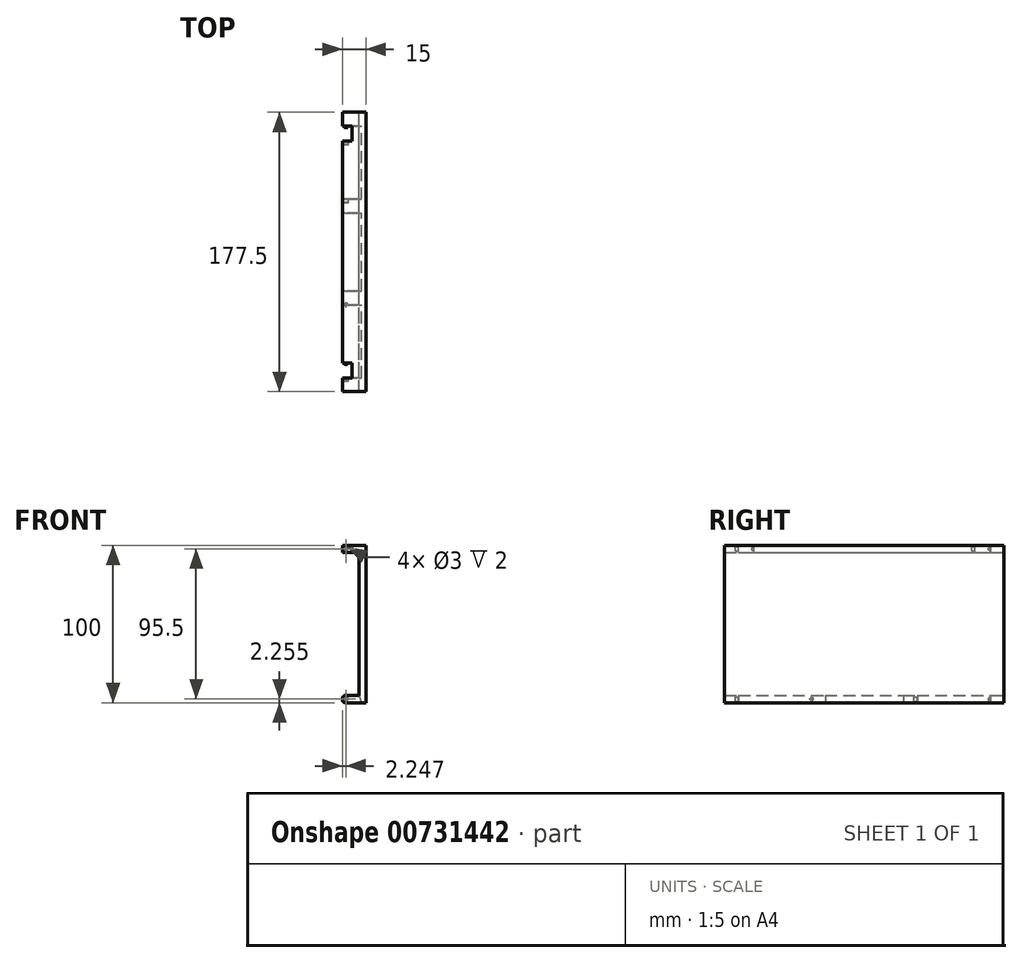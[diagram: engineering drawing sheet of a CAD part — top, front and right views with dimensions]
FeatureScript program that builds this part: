
annotation { "Feature Type Name" : "Feature", "Feature Type Description" : "" }
export const myFeature = defineFeature(function(context is Context, id is Id, definition is map)
    precondition{}
    {
        {
            var Q0;
            Q0=qCreatedBy(makeId("Front.planeOp"),FACE);
            var sketch = newSketch(context, id + "F0", { "sketchPlane" : qUnion([Q0])});
            skLineSegment(sketch, "E0", {"start": v(5.92, -29.22) * mm, "end": v(5.92, 61.78) * mm});
            skLineSegment(sketch, "E1", {"start": v(5.92, 61.78) * mm, "end": v(-4.58, 61.78) * mm});
            skLineSegment(sketch, "E2", {"start": v(-4.58, 61.78) * mm, "end": v(-4.58, 66.28) * mm});
            skLineSegment(sketch, "E3", {"start": v(-4.58, 66.28) * mm, "end": v(10.42, 66.28) * mm});
            skLineSegment(sketch, "E4", {"start": v(10.42, 66.28) * mm, "end": v(10.42, -33.72) * mm});
            skLineSegment(sketch, "E5", {"start": v(-4.58, 66.28) * mm, "end": v(-0.08, 66.28) * mm});
            skPoint(sketch, "E6.visualSharp", {"position": v(-0.08, -33.72) * mm});
            skPoint(sketch, "E7.visualSharp", {"position": v(-4.58, -29.22) * mm});
            skLineSegment(sketch, "E8", {"start": v(5.92, -29.22) * mm, "end": v(-2.88, -29.22) * mm});
            skLineSegment(sketch, "E9", {"start": v(0.67, -29.22) * mm, "end": v(0.67, -33.72) * mm});
            skCircle(sketch, "E10", {"center": v(-2.33, -31.47) * mm, "radius": 1.5 * mm});
            skCircle(sketch, "E11", {"center": v(-2.33, -31.47) * mm, "radius": 1.3 * mm});
            skCircle(sketch, "E12", {"center": v(-2.33, 64.03) * mm, "radius": 1.3 * mm});
            skCircle(sketch, "E13", {"center": v(-2.33, 64.03) * mm, "radius": 1.5 * mm});
            skLineSegment(sketch, "E14", {"start": v(-4.58, -31.47) * mm, "end": v(-4.58, -31.47) * mm});
            skPoint(sketch, "E15.visualSharp", {"position": v(-4.58, -33.72) * mm});
            skLineSegment(sketch, "E16", {"start": v(0.67, -33.72) * mm, "end": v(10.42, -33.72) * mm});
            skLineSegment(sketch, "E17", {"start": v(-4.58, -30.92) * mm, "end": v(-4.58, -32.02) * mm});
            skLineSegment(sketch, "E18", {"start": v(0.67, -33.72) * mm, "end": v(-2.88, -33.72) * mm});
            skArc(sketch, "E19.filletArc", {"start": v(-2.88, -29.22) * mm, "mid": v(-4.09, -29.71) * mm, "end": v(-4.58, -30.92) * mm});
            skArc(sketch, "E20.filletArc", {"start": v(-4.58, -32.02) * mm, "mid": v(-4.09, -33.22) * mm, "end": v(-2.88, -33.72) * mm});
            skLineSegment(sketch, "E21", {"start": v(5.92, -29.22) * mm, "end": v(5.92, -33.72) * mm});
            skLineSegment(sketch, "E22", {"start": v(5.92, -29.22) * mm, "end": v(7.53, -33.72) * mm});
            skLineSegment(sketch, "E23", {"start": v(7.53, -33.72) * mm, "end": v(10.42, -33.72) * mm});
            skLineSegment(sketch, "E24", {"start": v(1.42, 66.28) * mm, "end": v(1.42, 61.78) * mm});
            skSolve(sketch);
        }
        {
            var Q0;
            {var subQ0=sQuery(id+"F0.wireOp",EDGE,"E0");Q0=makeQuery(id+"F0.imprint","IMPRINT",FACE,{"disambiguationData":[TD([[makeQuery(id+"F0.imprint","IMPRINT",EDGE,{"derivedFrom":subQ0}),-1.0]])]});}
            var Q1;
            {var subQ0=sQuery(id+"F0.wireOp",EDGE,"E9");Q1=makeQuery(id+"F0.imprint","IMPRINT",FACE,{"disambiguationData":[TD([[makeQuery(id+"F0.imprint","IMPRINT",EDGE,{"derivedFrom":subQ0}),-1.0]])]});}
            var Q2;
            {var subQ2=sQuery(id+"F0.wireOp",EDGE,"E9");Q2=makeQuery(id+"F0.imprint","IMPRINT",FACE,{"disambiguationData":[TD([[makeQuery(id+"F0.imprint","IMPRINT",EDGE,{"derivedFrom":subQ2}),1.0]])]});}
            var Q3;
            {var subQ4=sQuery(id+"F0.wireOp",EDGE,"E21");Q3=makeQuery(id+"F0.imprint","IMPRINT",FACE,{"disambiguationData":[TD([[makeQuery(id+"F0.imprint","IMPRINT",EDGE,{"derivedFrom":subQ4}),1.0]])]});}
            var Q4;
            {var subQ3=sQuery(id+"F0.wireOp",EDGE,"E2");Q4=makeQuery(id+"F0.imprint","IMPRINT",FACE,{"disambiguationData":[TD([[makeQuery(id+"F0.imprint","IMPRINT",EDGE,{"derivedFrom":subQ3}),-1.0]])]});}
            extrude(context, id + "F1", {"entities" : qUnion([Q0, Q1, Q2, Q3, Q4]), "depth" : 177.5 * mm, "offsetDistance" : 25 * mm});
        }
        {
            var Q0;
            {var subQ2=sQuery(id+"F0.wireOp",EDGE,"E9");Q0=makeQuery(id+"F0.imprint","IMPRINT",FACE,{"disambiguationData":[TD([[makeQuery(id+"F0.imprint","IMPRINT",EDGE,{"derivedFrom":subQ2}),1.0]])]});}
            var Q1;
            {var subQ0=sQuery(id+"F0.wireOp",EDGE,"E9");Q1=makeQuery(id+"F0.imprint","IMPRINT",FACE,{"disambiguationData":[TD([[makeQuery(id+"F0.imprint","IMPRINT",EDGE,{"derivedFrom":subQ0}),-1.0]])]});}
            var Q2;
            {var subQ4=sQuery(id+"F0.wireOp",EDGE,"E21");Q2=makeQuery(id+"F0.imprint","IMPRINT",FACE,{"disambiguationData":[TD([[makeQuery(id+"F0.imprint","IMPRINT",EDGE,{"derivedFrom":subQ4}),1.0]])]});}
            extrude(context, id + "F2", {"entities" : qUnion([Q0, Q1, Q2]), "operationType" : NewBodyOperationType.REMOVE, "depth" : 168.7 * mm, "offsetDistance" : 25 * mm});
        }
        {
            var Q0;
            {var subQ2=sQuery(id+"F0.wireOp",EDGE,"E9");Q0=makeQuery(id+"F0.imprint","IMPRINT",FACE,{"disambiguationData":[TD([[makeQuery(id+"F0.imprint","IMPRINT",EDGE,{"derivedFrom":subQ2}),1.0]])]});}
            var Q1;
            {var subQ0=sQuery(id+"F0.wireOp",EDGE,"E9");Q1=makeQuery(id+"F0.imprint","IMPRINT",FACE,{"disambiguationData":[TD([[makeQuery(id+"F0.imprint","IMPRINT",EDGE,{"derivedFrom":subQ0}),-1.0]])]});}
            var Q2;
            {var subQ4=sQuery(id+"F0.wireOp",EDGE,"E21");Q2=makeQuery(id+"F0.imprint","IMPRINT",FACE,{"disambiguationData":[TD([[makeQuery(id+"F0.imprint","IMPRINT",EDGE,{"derivedFrom":subQ4}),1.0]])]});}
            extrude(context, id + "F3", {"entities" : qUnion([Q0, Q1, Q2]), "operationType" : NewBodyOperationType.ADD, "depth" : 122.3 * mm, "offsetDistance" : 25 * mm});
        }
        {
            var Q0;
            {var subQ2=sQuery(id+"F0.wireOp",EDGE,"E9");Q0=makeQuery(id+"F0.imprint","IMPRINT",FACE,{"disambiguationData":[TD([[makeQuery(id+"F0.imprint","IMPRINT",EDGE,{"derivedFrom":subQ2}),1.0]])]});}
            var Q1;
            {var subQ0=sQuery(id+"F0.wireOp",EDGE,"E9");Q1=makeQuery(id+"F0.imprint","IMPRINT",FACE,{"disambiguationData":[TD([[makeQuery(id+"F0.imprint","IMPRINT",EDGE,{"derivedFrom":subQ0}),-1.0]])]});}
            var Q2;
            {var subQ4=sQuery(id+"F0.wireOp",EDGE,"E21");Q2=makeQuery(id+"F0.imprint","IMPRINT",FACE,{"disambiguationData":[TD([[makeQuery(id+"F0.imprint","IMPRINT",EDGE,{"derivedFrom":subQ4}),1.0]])]});}
            extrude(context, id + "F4", {"entities" : qUnion([Q0, Q1, Q2]), "operationType" : NewBodyOperationType.REMOVE, "depth" : 113.5 * mm, "offsetDistance" : 25 * mm});
        }
        {
            var Q0;
            {var subQ2=sQuery(id+"F0.wireOp",EDGE,"E9");Q0=makeQuery(id+"F0.imprint","IMPRINT",FACE,{"disambiguationData":[TD([[makeQuery(id+"F0.imprint","IMPRINT",EDGE,{"derivedFrom":subQ2}),1.0]])]});}
            var Q1;
            {var subQ0=sQuery(id+"F0.wireOp",EDGE,"E9");Q1=makeQuery(id+"F0.imprint","IMPRINT",FACE,{"disambiguationData":[TD([[makeQuery(id+"F0.imprint","IMPRINT",EDGE,{"derivedFrom":subQ0}),-1.0]])]});}
            var Q2;
            {var subQ4=sQuery(id+"F0.wireOp",EDGE,"E21");Q2=makeQuery(id+"F0.imprint","IMPRINT",FACE,{"disambiguationData":[TD([[makeQuery(id+"F0.imprint","IMPRINT",EDGE,{"derivedFrom":subQ4}),1.0]])]});}
            extrude(context, id + "F5", {"entities" : qUnion([Q0, Q1, Q2]), "operationType" : NewBodyOperationType.ADD, "depth" : 64 * mm, "offsetDistance" : 25 * mm});
        }
        {
            var Q0;
            {var subQ2=sQuery(id+"F0.wireOp",EDGE,"E9");Q0=makeQuery(id+"F0.imprint","IMPRINT",FACE,{"disambiguationData":[TD([[makeQuery(id+"F0.imprint","IMPRINT",EDGE,{"derivedFrom":subQ2}),1.0]])]});}
            var Q1;
            {var subQ0=sQuery(id+"F0.wireOp",EDGE,"E9");Q1=makeQuery(id+"F0.imprint","IMPRINT",FACE,{"disambiguationData":[TD([[makeQuery(id+"F0.imprint","IMPRINT",EDGE,{"derivedFrom":subQ0}),-1.0]])]});}
            var Q2;
            {var subQ4=sQuery(id+"F0.wireOp",EDGE,"E21");Q2=makeQuery(id+"F0.imprint","IMPRINT",FACE,{"disambiguationData":[TD([[makeQuery(id+"F0.imprint","IMPRINT",EDGE,{"derivedFrom":subQ4}),1.0]])]});}
            extrude(context, id + "F6", {"entities" : qUnion([Q0, Q1, Q2]), "operationType" : NewBodyOperationType.REMOVE, "depth" : 55.2 * mm, "offsetDistance" : 25 * mm});
        }
        {
            var Q0;
            {var subQ2=sQuery(id+"F0.wireOp",EDGE,"E9");Q0=makeQuery(id+"F0.imprint","IMPRINT",FACE,{"disambiguationData":[TD([[makeQuery(id+"F0.imprint","IMPRINT",EDGE,{"derivedFrom":subQ2}),1.0]])]});}
            var Q1;
            {var subQ0=sQuery(id+"F0.wireOp",EDGE,"E9");Q1=makeQuery(id+"F0.imprint","IMPRINT",FACE,{"disambiguationData":[TD([[makeQuery(id+"F0.imprint","IMPRINT",EDGE,{"derivedFrom":subQ0}),-1.0]])]});}
            var Q2;
            {var subQ4=sQuery(id+"F0.wireOp",EDGE,"E21");Q2=makeQuery(id+"F0.imprint","IMPRINT",FACE,{"disambiguationData":[TD([[makeQuery(id+"F0.imprint","IMPRINT",EDGE,{"derivedFrom":subQ4}),1.0]])]});}
            extrude(context, id + "F7", {"entities" : qUnion([Q0, Q1, Q2]), "operationType" : NewBodyOperationType.ADD, "depth" : 8.8 * mm, "offsetDistance" : 25 * mm});
        }
        {
            var Q0;
            {var subQ3=sQuery(id+"F0.wireOp",EDGE,"E2");Q0=makeQuery(id+"F0.imprint","IMPRINT",FACE,{"disambiguationData":[TD([[makeQuery(id+"F0.imprint","IMPRINT",EDGE,{"derivedFrom":subQ3}),-1.0]])]});}
            extrude(context, id + "F8", {"entities" : qUnion([Q0]), "operationType" : NewBodyOperationType.REMOVE, "depth" : 168.7 * mm, "offsetDistance" : 25 * mm});
        }
        {
            var Q0;
            {var subQ3=sQuery(id+"F0.wireOp",EDGE,"E2");Q0=makeQuery(id+"F0.imprint","IMPRINT",FACE,{"disambiguationData":[TD([[makeQuery(id+"F0.imprint","IMPRINT",EDGE,{"derivedFrom":subQ3}),-1.0]])]});}
            extrude(context, id + "F9", {"entities" : qUnion([Q0]), "operationType" : NewBodyOperationType.ADD, "depth" : 159.1 * mm, "offsetDistance" : 25 * mm});
        }
        {
            var Q0;
            {var subQ3=sQuery(id+"F0.wireOp",EDGE,"E2");Q0=makeQuery(id+"F0.imprint","IMPRINT",FACE,{"disambiguationData":[TD([[makeQuery(id+"F0.imprint","IMPRINT",EDGE,{"derivedFrom":subQ3}),-1.0]])]});}
            extrude(context, id + "F10", {"entities" : qUnion([Q0]), "operationType" : NewBodyOperationType.REMOVE, "depth" : 18.4 * mm, "offsetDistance" : 25 * mm});
        }
        {
            var Q0;
            {var subQ3=sQuery(id+"F0.wireOp",EDGE,"E2");Q0=makeQuery(id+"F0.imprint","IMPRINT",FACE,{"disambiguationData":[TD([[makeQuery(id+"F0.imprint","IMPRINT",EDGE,{"derivedFrom":subQ3}),-1.0]])]});}
            extrude(context, id + "F11", {"entities" : qUnion([Q0]), "operationType" : NewBodyOperationType.ADD, "depth" : 8.8 * mm, "offsetDistance" : 25 * mm});
        }
        {
            var Q0;
            Q0=makeQuery(id+"F0.imprint","IMPRINT",FACE,{"disambiguationData":[TD([[makeQuery(id+"F0.imprint","IMPRINT",EDGE,{"derivedFrom":sQuery(id+"F0.wireOp",EDGE,"E10")}),1.0]])]});
            var Q1;
            Q1=makeQuery(id+"F0.imprint","IMPRINT",FACE,{"disambiguationData":[TD([[makeQuery(id+"F0.imprint","IMPRINT",EDGE,{"derivedFrom":sQuery(id+"F0.wireOp",EDGE,"E12")}),-1.0]])]});
            extrude(context, id + "F12", {"entities" : qUnion([Q0, Q1]), "operationType" : NewBodyOperationType.ADD, "depth" : 8.8 * mm, "offsetDistance" : 25 * mm});
        }
        {
            var Q0;
            Q0=makeQuery(id+"F0.imprint","IMPRINT",FACE,{"disambiguationData":[TD([[makeQuery(id+"F0.imprint","IMPRINT",EDGE,{"derivedFrom":sQuery(id+"F0.wireOp",EDGE,"E11")}),1.0]])]});
            var Q1;
            Q1=makeQuery(id+"F0.imprint","IMPRINT",FACE,{"disambiguationData":[TD([[makeQuery(id+"F0.imprint","IMPRINT",EDGE,{"derivedFrom":sQuery(id+"F0.wireOp",EDGE,"E12")}),1.0]])]});
            extrude(context, id + "F13", {"entities" : qUnion([Q0, Q1]), "operationType" : NewBodyOperationType.ADD, "depth" : 9.8 * mm, "offsetDistance" : 25 * mm});
        }
        {
            var Q0;
            Q0=makeQuery(id+"F13.opExtrude","CAP_EDGE",EDGE,{"disambiguationData":[OSD([sQuery(id+"F0.wireOp",EDGE,"E11")])],"isStart":false});
            fillet(context, id + "F14", {"entities" : qUnion([Q0]), "radius" : 1 * mm, "tangentPropagation" : true, "allowEdgeOverflow" : false});
        }
        {
            var Q0;
            Q0=makeQuery(id+"F6.boolean.opBoolean","COPY",FACE,{"derivedFrom":makeQuery(id+"F6.opExtrude","CAP_FACE",FACE,{"disambiguationData":[OSD([sQuery(id+"F0.wireOp",EDGE,"E8"),sQuery(id+"F0.wireOp",EDGE,"E10"),sQuery(id+"F0.wireOp",EDGE,"E16"),sQuery(id+"F0.wireOp",EDGE,"E17"),sQuery(id+"F0.wireOp",EDGE,"E18"),sQuery(id+"F0.wireOp",EDGE,"E19.filletArc"),sQuery(id+"F0.wireOp",EDGE,"E20.filletArc"),sQuery(id+"F0.wireOp",EDGE,"E22")])],"isStart":false})});
            var sketch = newSketch(context, id + "F15", { "sketchPlane" : qUnion([Q0])});
            skCircle(sketch, "E25", {"center": v(2.33, -31.47) * mm, "radius": 1.5 * mm});
            skCircle(sketch, "E26", {"center": v(2.33, -31.47) * mm, "radius": 1.3 * mm});
            skSolve(sketch);
        }
        {
            var Q0;
            Q0=makeQuery(id+"F15.imprint","IMPRINT",FACE,{"disambiguationData":[TD([[makeQuery(id+"F15.imprint","IMPRINT",EDGE,{"derivedFrom":sQuery(id+"F15.wireOp",EDGE,"E25")}),-1.0]])]});
            var Q1;
            Q1=makeQuery(id+"F15.imprint","IMPRINT",FACE,{"disambiguationData":[TD([[makeQuery(id+"F15.imprint","IMPRINT",EDGE,{"derivedFrom":sQuery(id+"F15.wireOp",EDGE,"E26")}),1.0]])]});
            extrude(context, id + "F16", {"entities" : qUnion([Q0, Q1]), "operationType" : NewBodyOperationType.ADD, "oppositeDirection" : true, "depth" : 8.8 * mm, "offsetDistance" : 25 * mm});
        }
        {
            var Q0;
            Q0=makeQuery(id+"F4.boolean.opBoolean","COPY",FACE,{"derivedFrom":makeQuery(id+"F4.opExtrude","CAP_FACE",FACE,{"disambiguationData":[OSD([sQuery(id+"F0.wireOp",EDGE,"E8"),sQuery(id+"F0.wireOp",EDGE,"E10"),sQuery(id+"F0.wireOp",EDGE,"E16"),sQuery(id+"F0.wireOp",EDGE,"E17"),sQuery(id+"F0.wireOp",EDGE,"E18"),sQuery(id+"F0.wireOp",EDGE,"E19.filletArc"),sQuery(id+"F0.wireOp",EDGE,"E20.filletArc"),sQuery(id+"F0.wireOp",EDGE,"E22")])],"isStart":false})});
            var sketch = newSketch(context, id + "F17", { "sketchPlane" : qUnion([Q0])});
            skCircle(sketch, "E27", {"center": v(2.33, -31.47) * mm, "radius": 1.5 * mm});
            skCircle(sketch, "E28", {"center": v(2.33, -31.47) * mm, "radius": 1.3 * mm});
            skSolve(sketch);
        }
        {
            var Q0;
            Q0=makeQuery(id+"F2.boolean.opBoolean","COPY",FACE,{"derivedFrom":makeQuery(id+"F2.opExtrude","CAP_FACE",FACE,{"disambiguationData":[OSD([sQuery(id+"F0.wireOp",EDGE,"E8"),sQuery(id+"F0.wireOp",EDGE,"E10"),sQuery(id+"F0.wireOp",EDGE,"E16"),sQuery(id+"F0.wireOp",EDGE,"E17"),sQuery(id+"F0.wireOp",EDGE,"E18"),sQuery(id+"F0.wireOp",EDGE,"E19.filletArc"),sQuery(id+"F0.wireOp",EDGE,"E20.filletArc"),sQuery(id+"F0.wireOp",EDGE,"E22")])],"isStart":false})});
            var sketch = newSketch(context, id + "F18", { "sketchPlane" : qUnion([Q0])});
            skCircle(sketch, "E29", {"center": v(2.33, -31.47) * mm, "radius": 1.5 * mm});
            skCircle(sketch, "E30", {"center": v(2.33, -31.47) * mm, "radius": 1.3 * mm});
            skSolve(sketch);
        }
        {
            var Q0;
            Q0=makeQuery(id+"F17.imprint","IMPRINT",FACE,{"disambiguationData":[TD([[makeQuery(id+"F17.imprint","IMPRINT",EDGE,{"derivedFrom":sQuery(id+"F17.wireOp",EDGE,"E27")}),-1.0]])]});
            var Q1;
            Q1=makeQuery(id+"F18.imprint","IMPRINT",FACE,{"disambiguationData":[TD([[makeQuery(id+"F18.imprint","IMPRINT",EDGE,{"derivedFrom":sQuery(id+"F18.wireOp",EDGE,"E30")}),1.0]])]});
            var Q2;
            Q2=makeQuery(id+"F18.imprint","IMPRINT",FACE,{"disambiguationData":[TD([[makeQuery(id+"F18.imprint","IMPRINT",EDGE,{"derivedFrom":sQuery(id+"F18.wireOp",EDGE,"E29")}),-1.0]])]});
            extrude(context, id + "F19", {"entities" : qUnion([Q0, Q1, Q2]), "operationType" : NewBodyOperationType.ADD, "oppositeDirection" : true, "depth" : 8.8 * mm, "offsetDistance" : 25 * mm});
        }
        {
            var Q0;
            Q0=makeQuery(id+"F17.imprint","IMPRINT",FACE,{"disambiguationData":[TD([[makeQuery(id+"F17.imprint","IMPRINT",EDGE,{"derivedFrom":sQuery(id+"F17.wireOp",EDGE,"E28")}),1.0]])]});
            extrude(context, id + "F20", {"entities" : qUnion([Q0]), "operationType" : NewBodyOperationType.ADD, "oppositeDirection" : true, "depth" : 9.8 * mm, "offsetDistance" : 25 * mm});
        }
        {
            var Q0;
            Q0=makeQuery(id+"F15.imprint","IMPRINT",FACE,{"disambiguationData":[TD([[makeQuery(id+"F15.imprint","IMPRINT",EDGE,{"derivedFrom":sQuery(id+"F15.wireOp",EDGE,"E25")}),-1.0]])]});
            var Q1;
            Q1=makeQuery(id+"F15.imprint","IMPRINT",FACE,{"disambiguationData":[TD([[makeQuery(id+"F15.imprint","IMPRINT",EDGE,{"derivedFrom":sQuery(id+"F15.wireOp",EDGE,"E26")}),1.0]])]});
            var Q2;
            Q2=makeQuery(id+"F18.imprint","IMPRINT",FACE,{"disambiguationData":[TD([[makeQuery(id+"F18.imprint","IMPRINT",EDGE,{"derivedFrom":sQuery(id+"F18.wireOp",EDGE,"E30")}),1.0]])]});
            var Q3;
            Q3=makeQuery(id+"F18.imprint","IMPRINT",FACE,{"disambiguationData":[TD([[makeQuery(id+"F18.imprint","IMPRINT",EDGE,{"derivedFrom":sQuery(id+"F18.wireOp",EDGE,"E29")}),-1.0]])]});
            extrude(context, id + "F21", {"entities" : qUnion([Q0, Q1, Q2, Q3]), "operationType" : NewBodyOperationType.REMOVE, "oppositeDirection" : true, "depth" : 2 * mm, "offsetDistance" : 25 * mm});
        }
        {
            var Q0;
            Q0=makeQuery(id+"F19.boolean.opBoolean","MERGE",FACE,{"derivedFrom":[makeQuery(id+"F1.opExtrude","CAP_FACE",FACE,{"disambiguationData":[OSD([sQuery(id+"F0.wireOp",EDGE,"E0"),sQuery(id+"F0.wireOp",EDGE,"E1"),sQuery(id+"F0.wireOp",EDGE,"E2"),sQuery(id+"F0.wireOp",EDGE,"E3"),sQuery(id+"F0.wireOp",EDGE,"E4"),sQuery(id+"F0.wireOp",EDGE,"E5"),sQuery(id+"F0.wireOp",EDGE,"E8"),sQuery(id+"F0.wireOp",EDGE,"E10"),sQuery(id+"F0.wireOp",EDGE,"E13"),sQuery(id+"F0.wireOp",EDGE,"E16"),sQuery(id+"F0.wireOp",EDGE,"E17"),sQuery(id+"F0.wireOp",EDGE,"E18"),sQuery(id+"F0.wireOp",EDGE,"E19.filletArc"),sQuery(id+"F0.wireOp",EDGE,"E20.filletArc"),sQuery(id+"F0.wireOp",EDGE,"E23")])],"isStart":false}),makeQuery(id+"F19.opExtrude","CAP_FACE",FACE,{"disambiguationData":[OSD([sQuery(id+"F18.wireOp",EDGE,"E29")])],"isStart":false})]});
            var sketch = newSketch(context, id + "F22", { "sketchPlane" : qUnion([Q0])});
            skCircle(sketch, "E31", {"center": v(-2.33, 64.03) * mm, "radius": 1.5 * mm});
            skSolve(sketch);
        }
        {
            var Q0;
            Q0=makeQuery(id+"F22.imprint","IMPRINT",FACE,{"disambiguationData":[TD([[makeQuery(id+"F22.imprint","IMPRINT",EDGE,{"derivedFrom":sQuery(id+"F22.wireOp",EDGE,"E31")}),1.0]])]});
            extrude(context, id + "F23", {"entities" : qUnion([Q0]), "operationType" : NewBodyOperationType.ADD, "oppositeDirection" : true, "depth" : 6.8 * mm, "offsetDistance" : 25 * mm});
        }
        {
            var Q0;
            Q0=makeQuery(id+"F9.opExtrude","CAP_FACE",FACE,{"disambiguationData":[OSD([sQuery(id+"F0.wireOp",EDGE,"E1"),sQuery(id+"F0.wireOp",EDGE,"E2"),sQuery(id+"F0.wireOp",EDGE,"E3"),sQuery(id+"F0.wireOp",EDGE,"E5"),sQuery(id+"F0.wireOp",EDGE,"E13"),sQuery(id+"F0.wireOp",EDGE,"E24")])],"isStart":false});
            var sketch = newSketch(context, id + "F24", { "sketchPlane" : qUnion([Q0])});
            skCircle(sketch, "E32", {"center": v(-2.33, 64.03) * mm, "radius": 1.3 * mm});
            skCircle(sketch, "E33", {"center": v(-2.33, 64.03) * mm, "radius": 1.5 * mm});
            skSolve(sketch);
        }
        {
            var Q0;
            Q0=makeQuery(id+"F24.imprint","IMPRINT",FACE,{"disambiguationData":[TD([[makeQuery(id+"F24.imprint","IMPRINT",EDGE,{"derivedFrom":sQuery(id+"F24.wireOp",EDGE,"E32")}),-1.0]])]});
            var Q1;
            Q1=makeQuery(id+"F24.imprint","IMPRINT",FACE,{"disambiguationData":[TD([[makeQuery(id+"F24.imprint","IMPRINT",EDGE,{"derivedFrom":sQuery(id+"F24.wireOp",EDGE,"E32")}),1.0]])]});
            extrude(context, id + "F25", {"entities" : qUnion([Q0, Q1]), "operationType" : NewBodyOperationType.ADD, "oppositeDirection" : true, "depth" : 138.7 * mm, "offsetDistance" : 25 * mm});
        }
        {
            var Q0;
            Q0=makeQuery(id+"F24.imprint","IMPRINT",FACE,{"disambiguationData":[TD([[makeQuery(id+"F24.imprint","IMPRINT",EDGE,{"derivedFrom":sQuery(id+"F24.wireOp",EDGE,"E32")}),1.0]])]});
            extrude(context, id + "F26", {"entities" : qUnion([Q0]), "operationType" : NewBodyOperationType.ADD, "depth" : 1 * mm, "offsetDistance" : 25 * mm});
        }
        {
            var Q0;
            Q0=makeQuery(id+"F26.opExtrude","CAP_EDGE",EDGE,{"disambiguationData":[OSD([sQuery(id+"F24.wireOp",EDGE,"E32")])],"isStart":false});
            var Q1;
            Q1=makeQuery(id+"F13.opExtrude","CAP_EDGE",EDGE,{"disambiguationData":[OSD([sQuery(id+"F0.wireOp",EDGE,"E12")])],"isStart":false});
            var Q2;
            Q2=makeQuery(id+"F20.opExtrude","CAP_EDGE",EDGE,{"disambiguationData":[OSD([sQuery(id+"F17.wireOp",EDGE,"E28")])],"isStart":false});
            fillet(context, id + "F27", {"entities" : qUnion([Q0, Q1, Q2]), "radius" : 1 * mm, "tangentPropagation" : true, "allowEdgeOverflow" : false});
        }
    });
